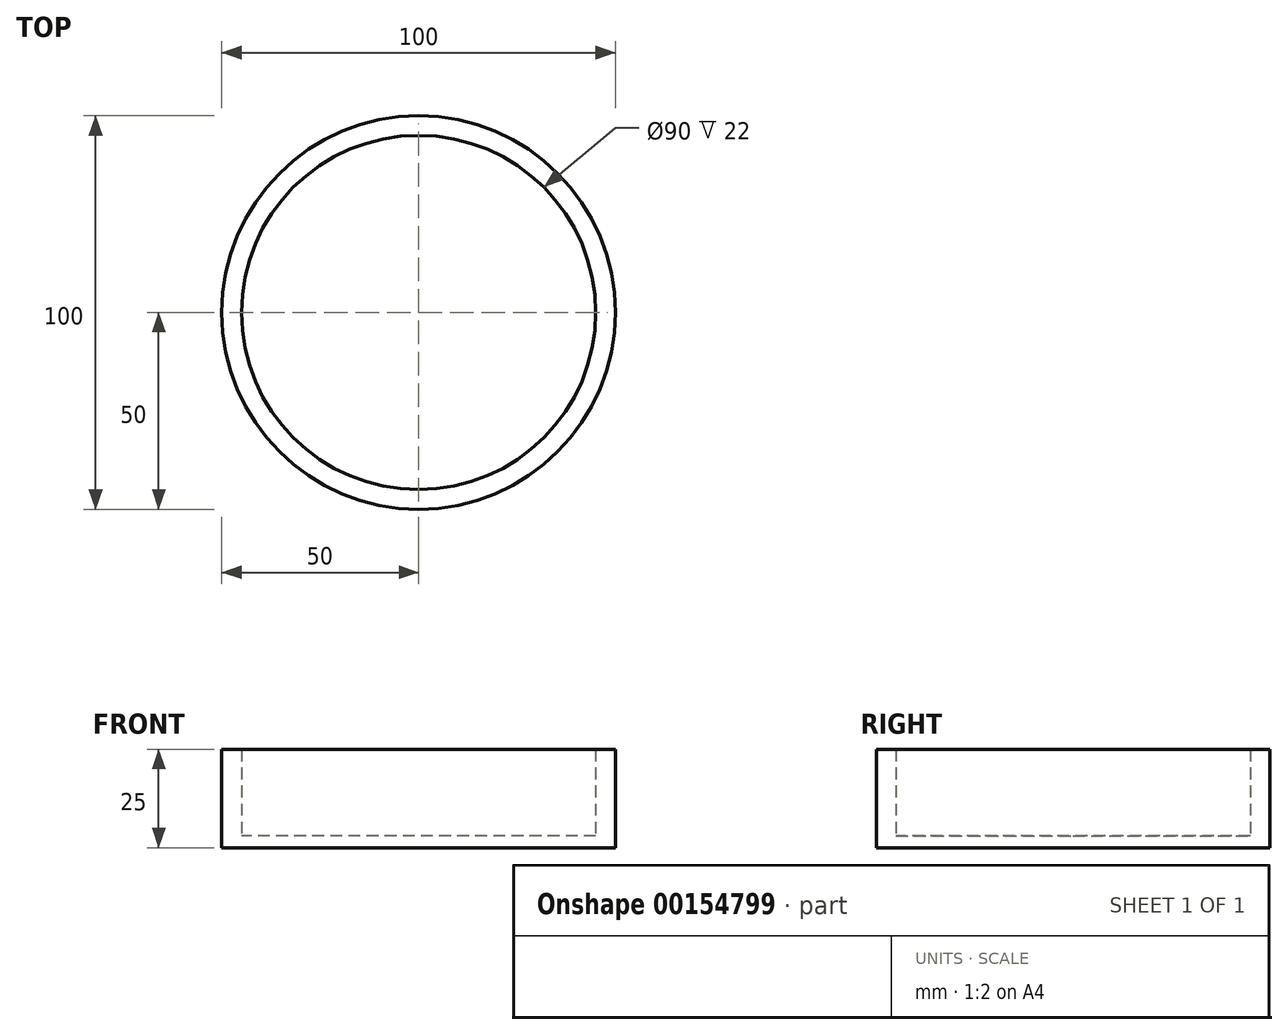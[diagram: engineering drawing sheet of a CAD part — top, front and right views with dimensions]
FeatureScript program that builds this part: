
annotation { "Feature Type Name" : "Feature", "Feature Type Description" : "" }
export const myFeature = defineFeature(function(context is Context, id is Id, definition is map)
    precondition{}
    {
        {
            var Q0;
            Q0=qCreatedBy(makeId("Top.planeOp"),FACE);
            var sketch = newSketch(context, id + "F0", { "sketchPlane" : qUnion([Q0])});
            skCircle(sketch, "E0", {"center": v(0, 0) * mm, "radius": 50 * mm});
            skCircle(sketch, "E1.0", {"center": v(0, 0) * mm, "radius": 45 * mm});
            skSolve(sketch);
        }
        {
            var Q0;
            Q0 = qSketchRegion(id + "F0", true);
            var Q1;
            Q1=makeQuery(id+"F0.imprint","IMPRINT",FACE,{"disambiguationData":[TD([[makeQuery(id+"F0.imprint","IMPRINT",EDGE,{"derivedFrom":sQuery(id+"F0.wireOp",EDGE,"E0")}),1.0]])]});
            extrude(context, id + "F1", {"entities" : qUnion([Q0, Q1]), "depth" : 25 * mm});
        }
        {
            var Q0;
            Q0=qCreatedBy(makeId("Top.planeOp"),FACE);
            var sketch = newSketch(context, id + "F2", { "sketchPlane" : qUnion([Q0])});
            skCircle(sketch, "E2", {"center": v(0, 0) * mm, "radius": 45.96 * mm});
            skSolve(sketch);
        }
        {
            var Q0;
            Q0 = qSketchRegion(id + "F2", true);
            extrude(context, id + "F3", {"entities" : qUnion([Q0]), "operationType" : NewBodyOperationType.ADD, "depth" : 3 * mm});
        }
    });
